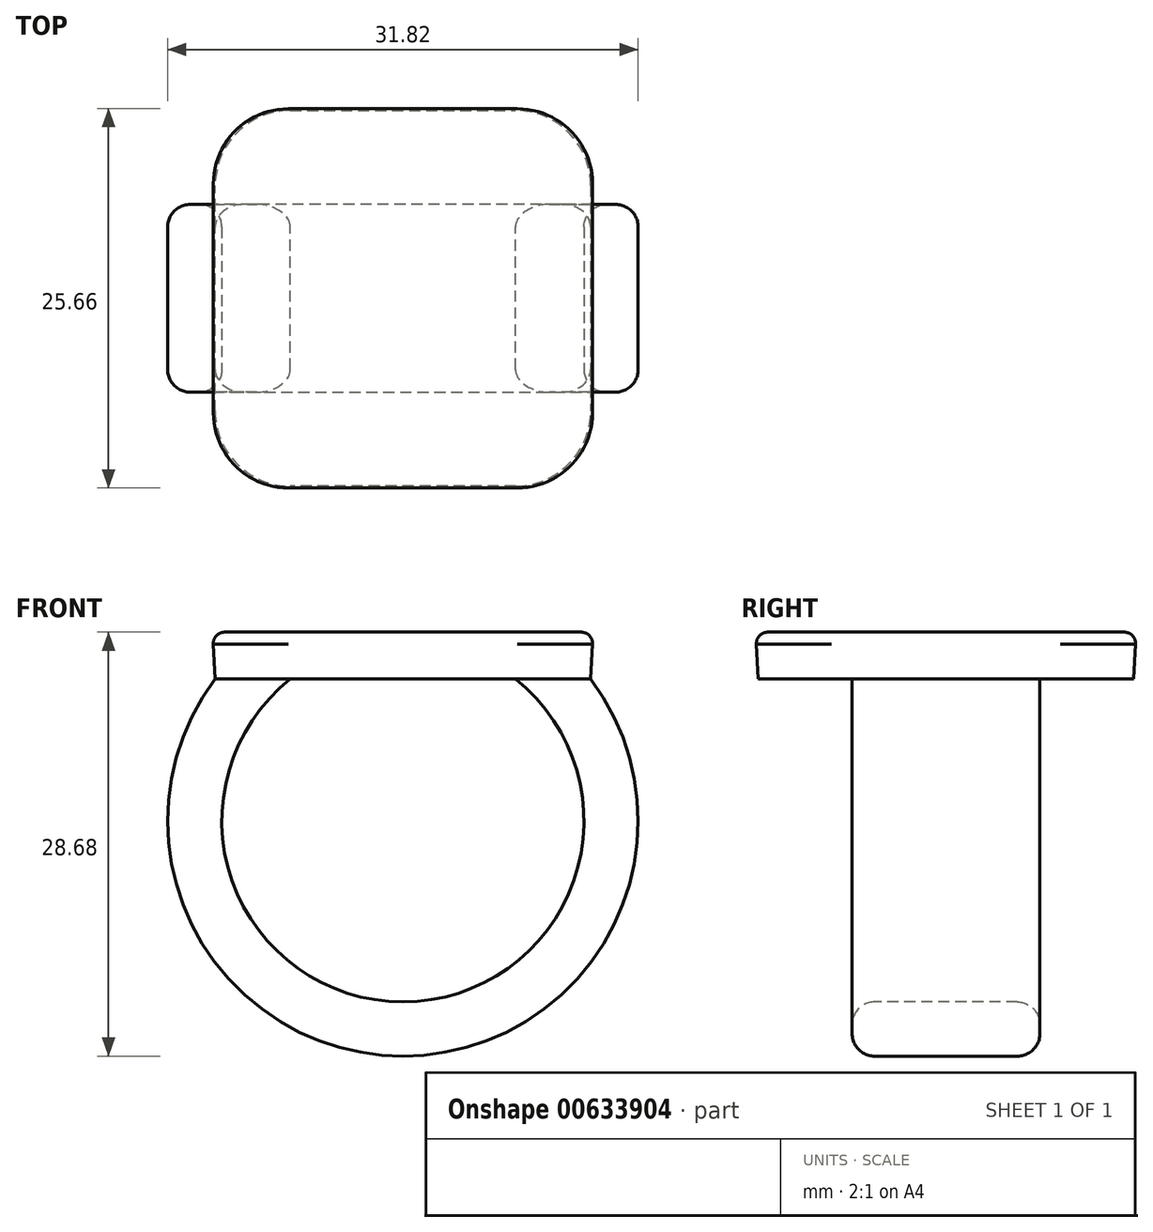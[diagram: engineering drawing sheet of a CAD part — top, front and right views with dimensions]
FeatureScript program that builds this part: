
annotation { "Feature Type Name" : "Feature", "Feature Type Description" : "" }
export const myFeature = defineFeature(function(context is Context, id is Id, definition is map)
    precondition{}
    {
        {
            var Q0;
            Q0=qCreatedBy(makeId("Top.planeOp"),FACE);
            var sketch = newSketch(context, id + "F0", { "sketchPlane" : qUnion([Q0])});
            skLineSegment(sketch, "E0.bottom", {"start": v(12.7, -12.7) * mm, "end": v(-12.7, -12.7) * mm});
            skLineSegment(sketch, "E0.top", {"start": v(12.7, 12.7) * mm, "end": v(-12.7, 12.7) * mm});
            skLineSegment(sketch, "E0.left", {"start": v(12.7, -12.7) * mm, "end": v(12.7, 12.7) * mm});
            skLineSegment(sketch, "E0.right", {"start": v(-12.7, -12.7) * mm, "end": v(-12.7, 12.7) * mm});
            skPoint(sketch, "E0.middle", {"position": v(0, 0) * mm});
            skSolve(sketch);
        }
        {
            var Q0;
            Q0 = qSketchRegion(id + "F0", true);
            extrude(context, id + "F1", {"entities" : qUnion([Q0]), "depth" : 3.17 * mm, "offsetDistance" : 25.4 * mm, "hasDraft" : true, "draftAngle" : 3 * degree});
        }
        {
            var Q0;
            Q0=qCreatedBy(makeId("Front.planeOp"),FACE);
            var sketch = newSketch(context, id + "F2", { "sketchPlane" : qUnion([Q0])});
            skArc(sketch, "E1", {"start": v(-10.16, 0) * mm, "mid": v(0, -23.56) * mm, "end": v(10.16, 0) * mm});
            skSolve(sketch);
        }
        {
            var Q0;
            Q0=makeQuery(id+"F1.opExtrude","CAP_FACE",FACE,{"disambiguationData":[OSD([sQuery(id+"F0.wireOp",EDGE,"E0.bottom"),sQuery(id+"F0.wireOp",EDGE,"E0.top"),sQuery(id+"F0.wireOp",EDGE,"E0.left"),sQuery(id+"F0.wireOp",EDGE,"E0.right")])],"isStart":true});
            var sketch = newSketch(context, id + "F3", { "sketchPlane" : qUnion([Q0])});
            skLineSegment(sketch, "E2.bottom", {"start": v(-7.62, 6.35) * mm, "end": v(-12.7, 6.35) * mm});
            skLineSegment(sketch, "E2.top", {"start": v(-7.62, -6.35) * mm, "end": v(-12.7, -6.35) * mm});
            skLineSegment(sketch, "E2.left", {"start": v(-7.62, 6.35) * mm, "end": v(-7.62, -6.35) * mm});
            skLineSegment(sketch, "E2.right", {"start": v(-12.7, 6.35) * mm, "end": v(-12.7, -6.35) * mm});
            skPoint(sketch, "E2.middle", {"position": v(-10.16, 0) * mm});
            skSolve(sketch);
        }
        {
            var Q0;
            Q0 = qSketchRegion(id + "F3", true);
            var Q1;
            Q1 = qConstructionFilter(qBodyType(qCreatedBy(id + "F2" ,EDGE), BodyType.WIRE), ConstructionObject.NO);
            sweep(context, id + "F4", {"operationType" : NewBodyOperationType.ADD, "profiles" : qUnion([Q0]), "path" : qUnion([Q1])});
        }
        {
            var Q0;
            Q0=qCreatedBy(makeId("Front.planeOp"),FACE);
            var sketch = newSketch(context, id + "F5", { "sketchPlane" : qUnion([Q0])});
            skLineSegment(sketch, "E3.0", {"start": v(10.16, 0) * mm, "end": v(7.62, 0) * mm});
            skArc(sketch, "E3.1", {"start": v(10.01, -2.54) * mm, "mid": v(8.9, -1.18) * mm, "end": v(7.62, 0) * mm});
            skLineSegment(sketch, "E3.2", {"start": v(10.01, -2.54) * mm, "end": v(10.16, 0) * mm});
            skPoint(sketch, "E4.orphan", {"position": v(10.01, -2.54) * mm});
            skPoint(sketch, "E5.orphan", {"position": v(-12.7, 0) * mm});
            skPoint(sketch, "E6.orphan", {"position": v(12.7, 0) * mm});
            skPoint(sketch, "E7.orphan", {"position": v(-7.62, 0) * mm});
            skSolve(sketch);
        }
        {
            var Q0;
            Q0=makeQuery(id+"F5.imprint","IMPRINT",FACE,{"disambiguationData":[TD([[makeQuery(id+"F5.imprint","IMPRINT",EDGE,{"derivedFrom":sQuery(id+"F5.wireOp",EDGE,"E3.0")}),1.0]])]});
            var Q1;
            Q1=makeQuery(id+"F4.opSweep","SWEPT_FACE",FACE,{"disambiguationData":[OSD([sQuery(id+"F2.wireOp",EDGE,"E1"),sQuery(id+"F3.wireOp",EDGE,"E2.bottom")])]});
            var Q2;
            Q2=makeQuery(id+"F4.opSweep","SWEPT_FACE",FACE,{"disambiguationData":[OSD([sQuery(id+"F2.wireOp",EDGE,"E1"),sQuery(id+"F3.wireOp",EDGE,"E2.top")])]});
            extrude(context, id + "F6", {"entities" : qUnion([Q0]), "operationType" : NewBodyOperationType.ADD, "endBound" : BoundingType.UP_TO_SURFACE, "depth" : 25.4 * mm, "endBoundEntityFace" : qUnion([Q1]), "offsetDistance" : 25.4 * mm, "hasSecondDirection" : true, "secondDirectionBound" : SecondDirectionBoundingType.UP_TO_SURFACE, "secondDirectionOppositeDirection" : true, "secondDirectionDepth" : 25.4 * mm, "secondDirectionBoundEntityFace" : qUnion([Q2])});
        }
        {
            var Q0;
            Q0=makeQuery(id+"F1.opExtrude","SWEPT_EDGE",EDGE,{"disambiguationData":[OSD([sQuery(id+"F0.wireOp",EDGE,"E0.bottom"),sQuery(id+"F0.wireOp",EDGE,"E0.left")])]});
            var Q1;
            Q1=makeQuery(id+"F1.opExtrude","SWEPT_EDGE",EDGE,{"disambiguationData":[OSD([sQuery(id+"F0.wireOp",EDGE,"E0.top"),sQuery(id+"F0.wireOp",EDGE,"E0.left")])]});
            var Q2;
            Q2=makeQuery(id+"F1.opExtrude","SWEPT_EDGE",EDGE,{"disambiguationData":[OSD([sQuery(id+"F0.wireOp",EDGE,"E0.top"),sQuery(id+"F0.wireOp",EDGE,"E0.right")])]});
            var Q3;
            Q3=makeQuery(id+"F1.opExtrude","SWEPT_EDGE",EDGE,{"disambiguationData":[OSD([sQuery(id+"F0.wireOp",EDGE,"E0.bottom"),sQuery(id+"F0.wireOp",EDGE,"E0.right")])]});
            fillet(context, id + "F7", {"entities" : qUnion([Q0, Q1, Q2, Q3]), "radius" : 5.08 * mm, "tangentPropagation" : true, "allowEdgeOverflow" : false});
        }
        {
            var Q0;
            Q0=makeQuery(id+"F4.opSweep","SWEPT_EDGE",EDGE,{"disambiguationData":[OSD([sQuery(id+"F0.wireOp",EDGE,"E0.right"),sQuery(id+"F2.wireOp",EDGE,"E1"),sQuery(id+"F3.wireOp",EDGE,"E2.bottom"),sQuery(id+"F3.wireOp",EDGE,"E2.right")])]});
            var Q1;
            Q1=makeQuery(id+"F4.opSweep","SWEPT_EDGE",EDGE,{"disambiguationData":[OSD([sQuery(id+"F0.wireOp",EDGE,"E0.right"),sQuery(id+"F2.wireOp",EDGE,"E1"),sQuery(id+"F3.wireOp",EDGE,"E2.top"),sQuery(id+"F3.wireOp",EDGE,"E2.right")])]});
            var Q2;
            {var subQ0=sQuery(id+"F3.wireOp",EDGE,"E2.top");var subQ1=sQuery(id+"F2.wireOp",EDGE,"E1");Q2=makeQuery(id+"F6.boolean.opBoolean","MERGE",EDGE,{"derivedFrom":[makeQuery(id+"F4.opSweep","SWEPT_EDGE",EDGE,{"disambiguationData":[OSD([subQ1,subQ0,sQuery(id+"F3.wireOp",EDGE,"E2.left")])]}),makeQuery(id+"F6.opExtrude","TWEAK_EDGE",EDGE,{"derivedFrom":[makeQuery(id+"F4.opSweep","SWEPT_FACE",FACE,{"disambiguationData":[OSD([subQ1,subQ0])]}),makeQuery(id+"F5.imprint","IMPRINT",EDGE,{"derivedFrom":sQuery(id+"F5.wireOp",EDGE,"E3.1")})]})]});}
            var Q3;
            {var subQ0=sQuery(id+"F3.wireOp",EDGE,"E2.bottom");var subQ1=sQuery(id+"F2.wireOp",EDGE,"E1");Q3=makeQuery(id+"F6.boolean.opBoolean","MERGE",EDGE,{"derivedFrom":[makeQuery(id+"F4.opSweep","SWEPT_EDGE",EDGE,{"disambiguationData":[OSD([subQ1,subQ0,sQuery(id+"F3.wireOp",EDGE,"E2.left")])]}),makeQuery(id+"F6.opExtrude","TWEAK_EDGE",EDGE,{"derivedFrom":[makeQuery(id+"F4.opSweep","SWEPT_FACE",FACE,{"disambiguationData":[OSD([subQ1,subQ0])]}),makeQuery(id+"F5.imprint","IMPRINT",EDGE,{"derivedFrom":sQuery(id+"F5.wireOp",EDGE,"E3.1")})]})]});}
            fillet(context, id + "F8", {"entities" : qUnion([Q0, Q1, Q2, Q3]), "radius" : 1.52 * mm, "tangentPropagation" : true, "allowEdgeOverflow" : false});
        }
        {
            var Q0;
            Q0=makeQuery(id+"F1.opExtrude","CAP_FACE",FACE,{"disambiguationData":[OSD([sQuery(id+"F0.wireOp",EDGE,"E0.bottom"),sQuery(id+"F0.wireOp",EDGE,"E0.top"),sQuery(id+"F0.wireOp",EDGE,"E0.left"),sQuery(id+"F0.wireOp",EDGE,"E0.right")])],"isStart":false});
            fillet(context, id + "F9", {"entities" : qUnion([Q0]), "radius" : 0.76 * mm, "tangentPropagation" : true, "allowEdgeOverflow" : false});
        }
    });
